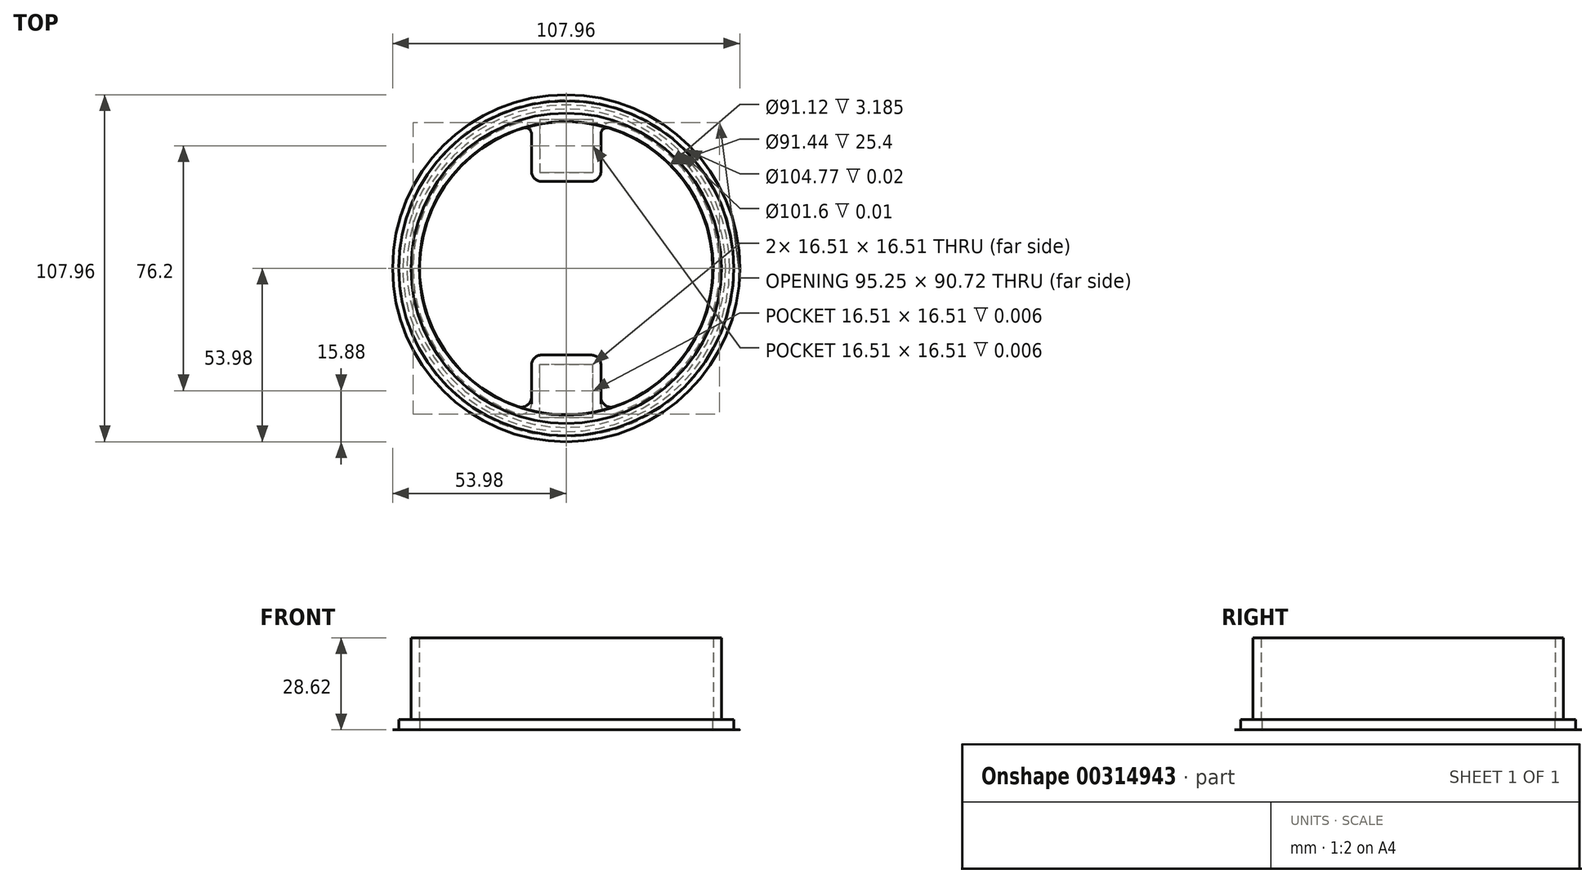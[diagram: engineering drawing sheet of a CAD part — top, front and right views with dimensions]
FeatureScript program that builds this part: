
annotation { "Feature Type Name" : "Feature", "Feature Type Description" : "" }
export const myFeature = defineFeature(function(context is Context, id is Id, definition is map)
    precondition{}
    {
        {
            var Q0;
            Q0=qCreatedBy(makeId("Top.planeOp"),FACE);
            var sketch = newSketch(context, id + "F0", { "sketchPlane" : qUnion([Q0])});
            skCircle(sketch, "E0", {"center": v(0, 0) * mm, "radius": 52.39 * mm});
            skCircle(sketch, "E1", {"center": v(0, 0) * mm, "radius": 53.98 * mm});
            skSolve(sketch);
        }
        {
            var Q0;
            Q0 = qSketchRegion(id + "F0", true);
            extrude(context, id + "F1", {"entities" : qUnion([Q0]), "depth" : 1 / 50.8 * mm});
        }
        {
            var Q0;
            Q0=makeQuery(id+"F1.opExtrude","CAP_FACE",FACE,{"disambiguationData":[OSD([sQuery(id+"F0.wireOp",EDGE,"E0"),sQuery(id+"F0.wireOp",EDGE,"E1")])],"isStart":false});
            var sketch = newSketch(context, id + "F2", { "sketchPlane" : qUnion([Q0])});
            skCircle(sketch, "E2.0", {"center": v(0, 0) * mm, "radius": 53.98 * mm});
            skArc(sketch, "E3.0", {"start": v(-14.97, 45.21) * mm, "mid": v(-47.62, 0) * mm, "end": v(-14.97, -45.21) * mm});
            skPoint(sketch, "E4.middle", {"position": v(0, 41.27) * mm});
            skPoint(sketch, "E5.orphan", {"position": v(-12.07, 48.74) * mm});
            skPoint(sketch, "E6.orphan", {"position": v(10.8, 51.42) * mm});
            skLineSegment(sketch, "E7.MirrorCS", {"start": v(-10.8, -42.2) * mm, "end": v(-10.8, -30.16) * mm});
            skArc(sketch, "E8.trimOffspring", {"start": v(14.97, -45.21) * mm, "mid": v(47.62, 0) * mm, "end": v(14.97, 45.21) * mm});
            skPoint(sketch, "E9.visualSharp", {"position": v(-10.8, -46.39) * mm});
            skArc(sketch, "E9.filletArc", {"start": v(-14.97, -45.21) * mm, "mid": v(-12.11, -44.77) * mm, "end": v(-10.8, -42.2) * mm});
            skPoint(sketch, "E10.visualSharp", {"position": v(-10.8, -31.13) * mm});
            skPoint(sketch, "E11.visualSharp", {"position": v(12.06, -32.23) * mm});
            skPoint(sketch, "E12.visualSharp", {"position": v(20.45, -43) * mm});
            skPoint(sketch, "E13.visualSharp", {"position": v(-10.8, 31.13) * mm});
            skPoint(sketch, "E14.visualSharp", {"position": v(-10.8, 46.39) * mm});
            skPoint(sketch, "E15.visualSharp", {"position": v(20.45, 43) * mm});
            skLineSegment(sketch, "E16", {"start": v(7.62, -26.99) * mm, "end": v(-7.62, -26.99) * mm});
            skPoint(sketch, "E17.visualSharp", {"position": v(7.88, -26.99) * mm});
            skPoint(sketch, "E18.visualSharp", {"position": v(-10.8, -26.99) * mm});
            skArc(sketch, "E18.filletArc", {"start": v(-7.62, -26.99) * mm, "mid": v(-9.87, -27.92) * mm, "end": v(-10.8, -30.16) * mm});
            skLineSegment(sketch, "E19.MirrorCS", {"start": v(7.62, 26.99) * mm, "end": v(-7.62, 26.99) * mm});
            skArc(sketch, "E20.MirrorCS", {"start": v(-7.62, 26.99) * mm, "mid": v(-9.87, 27.92) * mm, "end": v(-10.8, 30.16) * mm});
            skLineSegment(sketch, "E21.MirrorCS", {"start": v(-10.8, 42.2) * mm, "end": v(-10.8, 30.16) * mm});
            skLineSegment(sketch, "E22.MirrorCS", {"start": v(10.8, 42.2) * mm, "end": v(10.8, 30.16) * mm});
            skArc(sketch, "E23.MirrorCS", {"start": v(7.62, 26.99) * mm, "mid": v(9.87, 27.92) * mm, "end": v(10.8, 30.16) * mm});
            skArc(sketch, "E24.MirrorCS", {"start": v(7.62, -26.99) * mm, "mid": v(9.87, -27.92) * mm, "end": v(10.8, -30.16) * mm});
            skLineSegment(sketch, "E25.MirrorCS", {"start": v(10.8, -42.2) * mm, "end": v(10.8, -30.16) * mm});
            skArc(sketch, "E26.MirrorCS", {"start": v(14.97, -45.21) * mm, "mid": v(12.11, -44.77) * mm, "end": v(10.8, -42.2) * mm});
            skPoint(sketch, "E27.orphan", {"position": v(5.08, 26.99) * mm});
            skPoint(sketch, "E28.orphan", {"position": v(5.08, -26.99) * mm});
            skArc(sketch, "E29.MirrorCS", {"start": v(-14.97, 45.21) * mm, "mid": v(-12.11, 44.77) * mm, "end": v(-10.8, 42.2) * mm});
            skArc(sketch, "E30.MirrorCS", {"start": v(14.97, 45.21) * mm, "mid": v(12.11, 44.77) * mm, "end": v(10.8, 42.2) * mm});
            skSolve(sketch);
        }
        {
            var Q0;
            Q0 = qSketchRegion(id + "F2", true);
            extrude(context, id + "F3", {"entities" : qUnion([Q0]), "operationType" : NewBodyOperationType.ADD, "depth" : 1 / 101.6 * mm});
        }
        {
            var Q0;
            Q0=makeQuery(id+"F3.opExtrude","CAP_FACE",FACE,{"disambiguationData":[OSD([sQuery(id+"F2.wireOp",EDGE,"E2.0"),sQuery(id+"F2.wireOp",EDGE,"E3.0")])],"isStart":false});
            var sketch = newSketch(context, id + "F4", { "sketchPlane" : qUnion([Q0])});
            skCircle(sketch, "E31", {"center": v(0, 0) * mm, "radius": 50.8 * mm});
            skCircle(sketch, "E32.0", {"center": v(0, 0) * mm, "radius": 53.98 * mm});
            skSolve(sketch);
        }
        {
            var Q0;
            Q0 = qSketchRegion(id + "F4", true);
            extrude(context, id + "F5", {"entities" : qUnion([Q0]), "operationType" : NewBodyOperationType.ADD, "depth" : 1 / 101.6 * mm});
        }
        {
            var Q0;
            Q0=makeQuery(id+"F3.opExtrude","CAP_FACE",FACE,{"disambiguationData":[OSD([sQuery(id+"F2.wireOp",EDGE,"E2.0"),sQuery(id+"F2.wireOp",EDGE,"E3.0"),sQuery(id+"F2.wireOp",EDGE,"E4.top"),sQuery(id+"F2.wireOp",EDGE,"E4.left"),sQuery(id+"F2.wireOp",EDGE,"E4.right"),sQuery(id+"F2.wireOp",EDGE,"E7.MirrorCS"),sQuery(id+"F2.wireOp",EDGE,"14d7e438-5bb9-4d8e-acd8-ebce0bf1a9fc0.MirrorCS"),sQuery(id+"F2.wireOp",EDGE,"57ccc243-d271-415f-816b-320263d1c3790.MirrorCS"),sQuery(id+"F2.wireOp",EDGE,"E8.trimOffspring"),sQuery(id+"F2.wireOp",EDGE,"E9.filletArc"),sQuery(id+"F2.wireOp",EDGE,"E10.filletArc"),sQuery(id+"F2.wireOp",EDGE,"E11.filletArc"),sQuery(id+"F2.wireOp",EDGE,"E12.filletArc"),sQuery(id+"F2.wireOp",EDGE,"E13.filletArc"),sQuery(id+"F2.wireOp",EDGE,"E14.filletArc"),sQuery(id+"F2.wireOp",EDGE,"E15.filletArc"),sQuery(id+"F2.wireOp",EDGE,"87325a1d-47ca-4d5e-9cd2-0e4b37ab90e0.filletArc")])],"isStart":false});
            var sketch = newSketch(context, id + "F6", { "sketchPlane" : qUnion([Q0])});
            skLineSegment(sketch, "E33.bottom", {"start": v(8.25, 46.35) * mm, "end": v(-8.26, 46.35) * mm});
            skLineSegment(sketch, "E33.top", {"start": v(8.25, 29.84) * mm, "end": v(-8.26, 29.84) * mm});
            skLineSegment(sketch, "E33.left", {"start": v(8.25, 46.35) * mm, "end": v(8.25, 29.84) * mm});
            skLineSegment(sketch, "E33.right", {"start": v(-8.26, 46.35) * mm, "end": v(-8.26, 29.84) * mm});
            skPoint(sketch, "E33.middle", {"position": v(0, 38.1) * mm});
            skLineSegment(sketch, "E34.MirrorCS", {"start": v(-8.26, -46.35) * mm, "end": v(-8.26, -29.84) * mm});
            skLineSegment(sketch, "E35.MirrorCS", {"start": v(8.25, -46.35) * mm, "end": v(8.25, -29.84) * mm});
            skLineSegment(sketch, "E36.MirrorCS", {"start": v(8.25, -29.84) * mm, "end": v(-8.26, -29.84) * mm});
            skLineSegment(sketch, "E37.MirrorCS", {"start": v(8.25, -46.35) * mm, "end": v(-8.26, -46.35) * mm});
            skPoint(sketch, "E38.MirrorP", {"position": v(0, -38.1) * mm});
            skSolve(sketch);
        }
        {
            var Q0;
            Q0 = qSketchRegion(id + "F6", true);
            extrude(context, id + "F7", {"entities" : qUnion([Q0]), "operationType" : NewBodyOperationType.REMOVE, "oppositeDirection" : true, "depth" : 1 / 152.4 * mm});
        }
        {
            var Q0;
            Q0=makeQuery(id+"F5.opExtrude","CAP_FACE",FACE,{"disambiguationData":[OSD([sQuery(id+"F4.wireOp",EDGE,"E31"),sQuery(id+"F4.wireOp",EDGE,"E32.0")])],"isStart":false});
            var sketch = newSketch(context, id + "F8", { "sketchPlane" : qUnion([Q0])});
            skCircle(sketch, "E39.0", {"center": v(0, 0) * mm, "radius": 49.53 * mm});
            skArc(sketch, "E40.0", {"start": v(-10.8, 41.77) * mm, "mid": v(-11.57, 43.3) * mm, "end": v(-13.25, 43.6) * mm});
            skLineSegment(sketch, "E40.7", {"start": v(-10.8, -40.02) * mm, "end": v(-10.8, -30.16) * mm});
            skLineSegment(sketch, "E40.10", {"start": v(10.8, -40.02) * mm, "end": v(10.8, -30.16) * mm});
            skArc(sketch, "E40.13", {"start": v(13.25, 43.6) * mm, "mid": v(11.57, 43.3) * mm, "end": v(10.8, 41.77) * mm});
            skLineSegment(sketch, "E41", {"start": v(-7.62, -26.99) * mm, "end": v(7.62, -26.99) * mm});
            skLineSegment(sketch, "E42.MirrorCS", {"start": v(-7.62, 26.99) * mm, "end": v(7.62, 26.99) * mm});
            skLineSegment(sketch, "E43.MirrorCS", {"start": v(-10.8, 41.77) * mm, "end": v(-10.8, 30.16) * mm});
            skLineSegment(sketch, "E44.MirrorCS", {"start": v(10.8, 41.77) * mm, "end": v(10.8, 30.16) * mm});
            skPoint(sketch, "E45.visualSharp", {"position": v(-10.8, -26.99) * mm});
            skArc(sketch, "E45.filletArc", {"start": v(-7.62, -26.99) * mm, "mid": v(-9.87, -27.92) * mm, "end": v(-10.8, -30.16) * mm});
            skPoint(sketch, "E46.visualSharp", {"position": v(10.8, -26.99) * mm});
            skArc(sketch, "E46.filletArc", {"start": v(10.8, -30.16) * mm, "mid": v(9.87, -27.92) * mm, "end": v(7.62, -26.99) * mm});
            skPoint(sketch, "E47.visualSharp", {"position": v(10.8, 26.99) * mm});
            skArc(sketch, "E47.filletArc", {"start": v(7.62, 26.99) * mm, "mid": v(9.87, 27.92) * mm, "end": v(10.8, 30.16) * mm});
            skPoint(sketch, "E48.visualSharp", {"position": v(-10.8, 26.99) * mm});
            skArc(sketch, "E48.filletArc", {"start": v(-10.8, 30.16) * mm, "mid": v(-9.87, 27.92) * mm, "end": v(-7.62, 26.99) * mm});
            skArc(sketch, "E49", {"start": v(-13.25, 43.6) * mm, "mid": v(-45.55, 0.93) * mm, "end": v(-15.02, -43.02) * mm});
            skPoint(sketch, "E50.orphan", {"position": v(-10.8, -41.36) * mm});
            skPoint(sketch, "E51.orphan", {"position": v(10.8, -41.77) * mm});
            skArc(sketch, "E52.trimOffspring", {"start": v(15.02, -43.02) * mm, "mid": v(45.55, 0.93) * mm, "end": v(13.25, 43.6) * mm});
            skPoint(sketch, "E53.visualSharp", {"position": v(-10.8, -44.26) * mm});
            skArc(sketch, "E53.filletArc", {"start": v(-15.02, -43.02) * mm, "mid": v(-12.13, -42.6) * mm, "end": v(-10.8, -40.02) * mm});
            skPoint(sketch, "E54.visualSharp", {"position": v(10.8, -44.26) * mm});
            skArc(sketch, "E54.filletArc", {"start": v(10.8, -40.02) * mm, "mid": v(12.13, -42.6) * mm, "end": v(15.02, -43.02) * mm});
            skPoint(sketch, "E55.orphan", {"position": v(-10.8, 41.36) * mm});
            skSolve(sketch);
        }
        {
            var Q0;
            Q0 = qSketchRegion(id + "F8", true);
            extrude(context, id + "F9", {"entities" : qUnion([Q0]), "operationType" : NewBodyOperationType.ADD, "depth" : 1 / 101.6 * mm});
        }
        {
            var Q0;
            Q0=makeQuery(id+"F9.opExtrude","CAP_FACE",FACE,{"disambiguationData":[OSD([sQuery(id+"F8.wireOp",EDGE,"E39.0"),sQuery(id+"F8.wireOp",EDGE,"E40.0"),sQuery(id+"F8.wireOp",EDGE,"E40.1"),sQuery(id+"F8.wireOp",EDGE,"E40.2"),sQuery(id+"F8.wireOp",EDGE,"E40.3"),sQuery(id+"F8.wireOp",EDGE,"E40.4"),sQuery(id+"F8.wireOp",EDGE,"E40.5"),sQuery(id+"F8.wireOp",EDGE,"E40.6"),sQuery(id+"F8.wireOp",EDGE,"E40.7"),sQuery(id+"F8.wireOp",EDGE,"E40.8"),sQuery(id+"F8.wireOp",EDGE,"E40.9"),sQuery(id+"F8.wireOp",EDGE,"E40.10"),sQuery(id+"F8.wireOp",EDGE,"E40.11"),sQuery(id+"F8.wireOp",EDGE,"E40.12"),sQuery(id+"F8.wireOp",EDGE,"E40.13"),sQuery(id+"F8.wireOp",EDGE,"E40.14"),sQuery(id+"F8.wireOp",EDGE,"E40.15")])],"isStart":false});
            var sketch = newSketch(context, id + "F10", { "sketchPlane" : qUnion([Q0])});
            skCircle(sketch, "E56", {"center": v(0, 0) * mm, "radius": 52.07 * mm});
            skCircle(sketch, "E57", {"center": v(0, 0) * mm, "radius": 45.56 * mm});
            skSolve(sketch);
        }
        {
            var Q0;
            Q0 = qSketchRegion(id + "F10", true);
            extrude(context, id + "F11", {"entities" : qUnion([Q0]), "operationType" : NewBodyOperationType.ADD, "depth" : 3.17 * mm});
        }
        {
            var Q0;
            Q0=makeQuery(id+"F11.opExtrude","CAP_FACE",FACE,{"disambiguationData":[OSD([sQuery(id+"F10.wireOp",EDGE,"E56"),sQuery(id+"F10.wireOp",EDGE,"E57")])],"isStart":false});
            var sketch = newSketch(context, id + "F12", { "sketchPlane" : qUnion([Q0])});
            skCircle(sketch, "E58", {"center": v(0, 0) * mm, "radius": 48.26 * mm});
            skCircle(sketch, "E59", {"center": v(0, 0) * mm, "radius": 45.72 * mm});
            skSolve(sketch);
        }
        {
            var Q0;
            Q0 = qSketchRegion(id + "F12", true);
            extrude(context, id + "F13", {"entities" : qUnion([Q0]), "operationType" : NewBodyOperationType.ADD, "depth" : 25.4 * mm});
        }
        {
            var Q0;
            Q0=makeQuery(id+"F9.opExtrude","CAP_FACE",FACE,{"disambiguationData":[OSD([sQuery(id+"F8.wireOp",EDGE,"E39.0"),sQuery(id+"F8.wireOp",EDGE,"E40.0"),sQuery(id+"F8.wireOp",EDGE,"E40.1"),sQuery(id+"F8.wireOp",EDGE,"E40.2"),sQuery(id+"F8.wireOp",EDGE,"E40.3"),sQuery(id+"F8.wireOp",EDGE,"E40.4"),sQuery(id+"F8.wireOp",EDGE,"E40.5"),sQuery(id+"F8.wireOp",EDGE,"E40.6"),sQuery(id+"F8.wireOp",EDGE,"E40.7"),sQuery(id+"F8.wireOp",EDGE,"E40.8"),sQuery(id+"F8.wireOp",EDGE,"E40.9"),sQuery(id+"F8.wireOp",EDGE,"E40.10"),sQuery(id+"F8.wireOp",EDGE,"E40.11"),sQuery(id+"F8.wireOp",EDGE,"E40.12"),sQuery(id+"F8.wireOp",EDGE,"E40.13"),sQuery(id+"F8.wireOp",EDGE,"E40.14"),sQuery(id+"F8.wireOp",EDGE,"E40.15")])],"isStart":true});
            var sketch = newSketch(context, id + "F14", { "sketchPlane" : qUnion([Q0])});
            skLineSegment(sketch, "E60.bottom", {"start": v(-8.26, -46.35) * mm, "end": v(8.26, -46.35) * mm});
            skLineSegment(sketch, "E60.top", {"start": v(-8.26, -29.84) * mm, "end": v(8.26, -29.84) * mm});
            skLineSegment(sketch, "E60.left", {"start": v(-8.26, -46.35) * mm, "end": v(-8.26, -29.84) * mm});
            skLineSegment(sketch, "E60.right", {"start": v(8.26, -46.35) * mm, "end": v(8.26, -29.84) * mm});
            skPoint(sketch, "E60.middle", {"position": v(0, -38.1) * mm});
            skPoint(sketch, "E60.middle.positionSnap0", {"position": v(10.8, -38.1) * mm});
            skPoint(sketch, "E60.centerSnap0", {"position": v(10.8, -38.1) * mm});
            skPoint(sketch, "E61.MirrorP", {"position": v(10.8, 38.1) * mm});
            skLineSegment(sketch, "E62.MirrorCS", {"start": v(8.25, 46.35) * mm, "end": v(8.25, 29.84) * mm});
            skLineSegment(sketch, "E63.MirrorCS", {"start": v(-8.26, 46.35) * mm, "end": v(-8.26, 29.84) * mm});
            skLineSegment(sketch, "E64.MirrorCS", {"start": v(-8.26, 29.84) * mm, "end": v(8.26, 29.84) * mm});
            skLineSegment(sketch, "E65.MirrorCS", {"start": v(-8.26, 46.35) * mm, "end": v(8.26, 46.35) * mm});
            skPoint(sketch, "E66.MirrorP", {"position": v(0, 38.1) * mm});
            skSolve(sketch);
        }
        {
            var Q0;
            Q0 = qSketchRegion(id + "F14", true);
            extrude(context, id + "F15", {"entities" : qUnion([Q0]), "operationType" : NewBodyOperationType.REMOVE, "oppositeDirection" : true, "depth" : 1 / 152.4 * mm});
        }
    });
